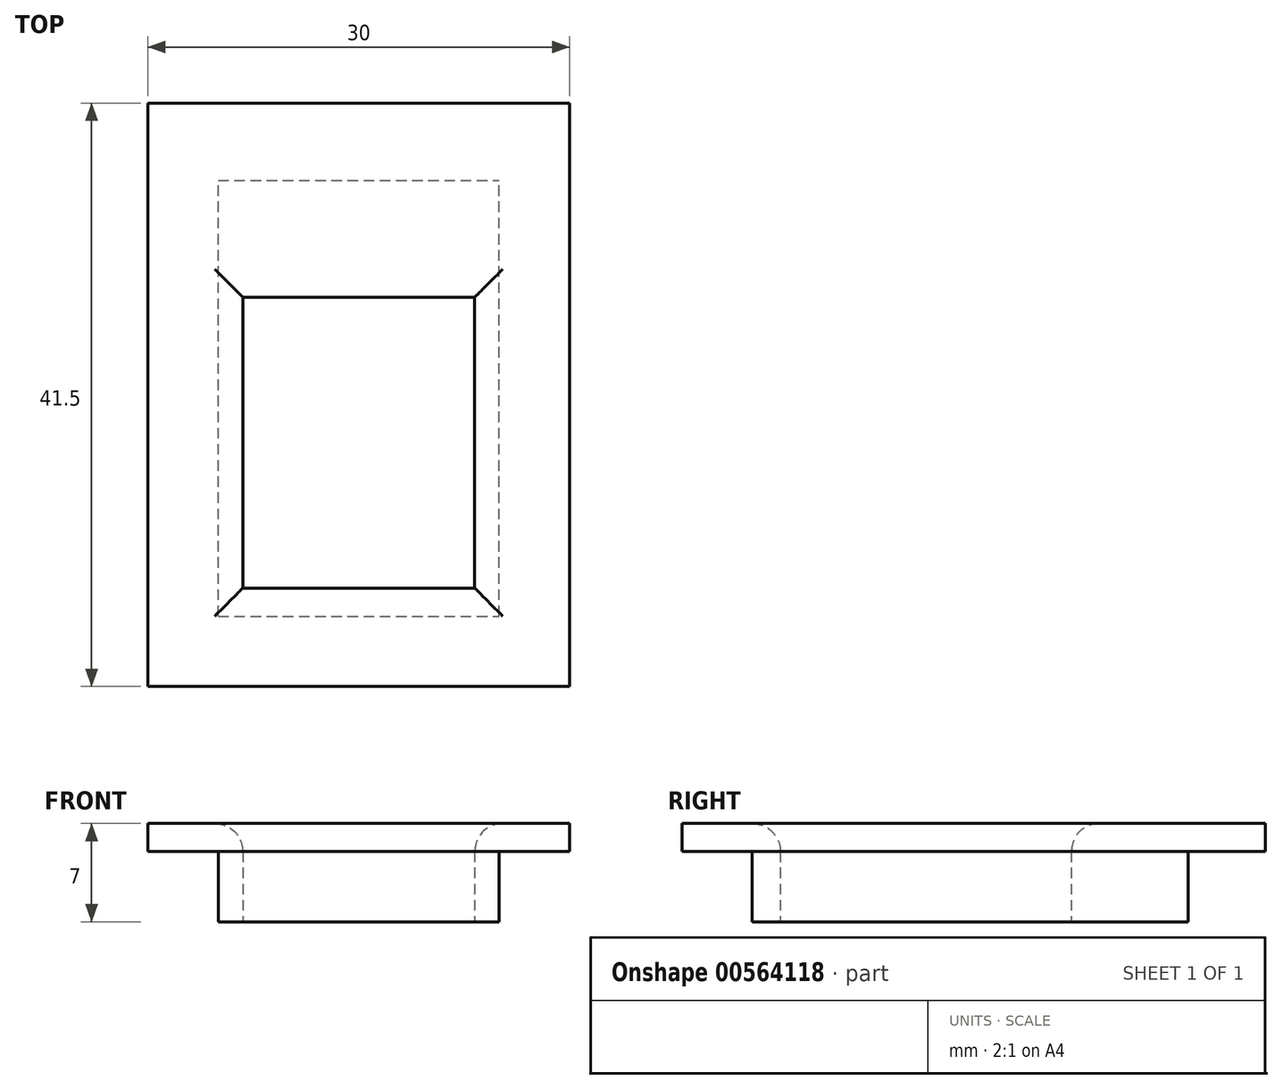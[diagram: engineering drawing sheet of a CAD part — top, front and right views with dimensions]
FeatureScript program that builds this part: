
annotation { "Feature Type Name" : "Feature", "Feature Type Description" : "" }
export const myFeature = defineFeature(function(context is Context, id is Id, definition is map)
    precondition{}
    {
        {
            var Q0;
            Q0=qCreatedBy(makeId("Top.planeOp"),FACE);
            var sketch = newSketch(context, id + "F0", { "sketchPlane" : qUnion([Q0])});
            skLineSegment(sketch, "E0.bottom", {"start": v(-14.79, 19.32) * mm, "end": v(15.21, 19.32) * mm});
            skLineSegment(sketch, "E0.top", {"start": v(-14.79, -22.18) * mm, "end": v(15.21, -22.18) * mm});
            skLineSegment(sketch, "E0.left", {"start": v(-14.79, 19.32) * mm, "end": v(-14.79, -22.18) * mm});
            skLineSegment(sketch, "E0.right", {"start": v(15.21, 19.32) * mm, "end": v(15.21, -22.18) * mm});
            skSolve(sketch);
        }
        {
            var Q0;
            Q0=makeQuery(id+"F0.imprint","IMPRINT",FACE,{"disambiguationData":[TD([[makeQuery(id+"F0.imprint","IMPRINT",EDGE,{"derivedFrom":sQuery(id+"F0.wireOp",EDGE,"E0.bottom")}),-1.0]])]});
            extrude(context, id + "F1", {"entities" : qUnion([Q0]), "depth" : 2 * mm, "offsetDistance" : 25 * mm});
        }
        {
            var Q0;
            Q0=makeQuery(id+"F1.opExtrude","CAP_FACE",FACE,{"disambiguationData":[OSD([sQuery(id+"F0.wireOp",EDGE,"E0.bottom"),sQuery(id+"F0.wireOp",EDGE,"E0.top"),sQuery(id+"F0.wireOp",EDGE,"E0.left"),sQuery(id+"F0.wireOp",EDGE,"E0.right")])],"isStart":true});
            var sketch = newSketch(context, id + "F2", { "sketchPlane" : qUnion([Q0])});
            skLineSegment(sketch, "E1.bottom", {"start": v(-9.79, 17.18) * mm, "end": v(10.21, 17.18) * mm});
            skLineSegment(sketch, "E1.top", {"start": v(-9.79, -13.82) * mm, "end": v(10.21, -13.82) * mm});
            skLineSegment(sketch, "E1.left", {"start": v(-9.79, 17.18) * mm, "end": v(-9.79, -13.82) * mm});
            skLineSegment(sketch, "E1.right", {"start": v(10.21, 17.18) * mm, "end": v(10.21, -13.82) * mm});
            skSolve(sketch);
        }
        {
            var Q0;
            Q0=makeQuery(id+"F2.imprint","IMPRINT",FACE,{"disambiguationData":[TD([[makeQuery(id+"F2.imprint","IMPRINT",EDGE,{"derivedFrom":sQuery(id+"F2.wireOp",EDGE,"E1.bottom")}),-1.0]])]});
            extrude(context, id + "F3", {"entities" : qUnion([Q0]), "operationType" : NewBodyOperationType.ADD, "depth" : 5 * mm, "offsetDistance" : 25 * mm});
        }
        {
            var Q0;
            Q0=makeQuery(id+"F3.opExtrude","CAP_FACE",FACE,{"disambiguationData":[OSD([sQuery(id+"F2.wireOp",EDGE,"E1.bottom"),sQuery(id+"F2.wireOp",EDGE,"E1.top"),sQuery(id+"F2.wireOp",EDGE,"E1.left"),sQuery(id+"F2.wireOp",EDGE,"E1.right")])],"isStart":false});
            var sketch = newSketch(context, id + "F4", { "sketchPlane" : qUnion([Q0])});
            skLineSegment(sketch, "E2.bottom", {"start": v(-8.04, 15.18) * mm, "end": v(8.46, 15.18) * mm});
            skLineSegment(sketch, "E2.top", {"start": v(-8.04, -5.52) * mm, "end": v(8.46, -5.52) * mm});
            skLineSegment(sketch, "E2.left", {"start": v(-8.04, 15.18) * mm, "end": v(-8.04, -5.52) * mm});
            skLineSegment(sketch, "E2.right", {"start": v(8.46, 15.18) * mm, "end": v(8.46, -5.52) * mm});
            skSolve(sketch);
        }
        {
            var Q0;
            Q0=makeQuery(id+"F4.imprint","IMPRINT",FACE,{"disambiguationData":[TD([[makeQuery(id+"F4.imprint","IMPRINT",EDGE,{"derivedFrom":sQuery(id+"F4.wireOp",EDGE,"E2.bottom")}),-1.0]])]});
            extrude(context, id + "F5", {"entities" : qUnion([Q0]), "operationType" : NewBodyOperationType.REMOVE, "oppositeDirection" : true, "depth" : 25 * mm, "offsetDistance" : 25 * mm});
        }
        {
            var Q0;
            Q0=makeQuery(id+"F5.boolean.opBoolean","INTERSECT",EDGE,{"derivedFrom":[makeQuery(id+"F1.opExtrude","CAP_FACE",FACE,{"disambiguationData":[OSD([sQuery(id+"F0.wireOp",EDGE,"E0.bottom"),sQuery(id+"F0.wireOp",EDGE,"E0.top"),sQuery(id+"F0.wireOp",EDGE,"E0.left"),sQuery(id+"F0.wireOp",EDGE,"E0.right")])],"isStart":false}),makeQuery(id+"F5.opExtrude","SWEPT_FACE",FACE,{"disambiguationData":[OSD([sQuery(id+"F4.wireOp",EDGE,"E2.right")])]})]});
            var Q1;
            Q1=makeQuery(id+"F5.boolean.opBoolean","INTERSECT",EDGE,{"derivedFrom":[makeQuery(id+"F1.opExtrude","CAP_FACE",FACE,{"disambiguationData":[OSD([sQuery(id+"F0.wireOp",EDGE,"E0.bottom"),sQuery(id+"F0.wireOp",EDGE,"E0.top"),sQuery(id+"F0.wireOp",EDGE,"E0.left"),sQuery(id+"F0.wireOp",EDGE,"E0.right")])],"isStart":false}),makeQuery(id+"F5.opExtrude","SWEPT_FACE",FACE,{"disambiguationData":[OSD([sQuery(id+"F4.wireOp",EDGE,"E2.top")])]})]});
            var Q2;
            Q2=makeQuery(id+"F5.boolean.opBoolean","INTERSECT",EDGE,{"derivedFrom":[makeQuery(id+"F1.opExtrude","CAP_FACE",FACE,{"disambiguationData":[OSD([sQuery(id+"F0.wireOp",EDGE,"E0.bottom"),sQuery(id+"F0.wireOp",EDGE,"E0.top"),sQuery(id+"F0.wireOp",EDGE,"E0.left"),sQuery(id+"F0.wireOp",EDGE,"E0.right")])],"isStart":false}),makeQuery(id+"F5.opExtrude","SWEPT_FACE",FACE,{"disambiguationData":[OSD([sQuery(id+"F4.wireOp",EDGE,"E2.left")])]})]});
            var Q3;
            Q3=makeQuery(id+"F5.boolean.opBoolean","INTERSECT",EDGE,{"derivedFrom":[makeQuery(id+"F1.opExtrude","CAP_FACE",FACE,{"disambiguationData":[OSD([sQuery(id+"F0.wireOp",EDGE,"E0.bottom"),sQuery(id+"F0.wireOp",EDGE,"E0.top"),sQuery(id+"F0.wireOp",EDGE,"E0.left"),sQuery(id+"F0.wireOp",EDGE,"E0.right")])],"isStart":false}),makeQuery(id+"F5.opExtrude","SWEPT_FACE",FACE,{"disambiguationData":[OSD([sQuery(id+"F4.wireOp",EDGE,"E2.bottom")])]})]});
            fillet(context, id + "F6", {"entities" : qUnion([Q0, Q1, Q2, Q3]), "radius" : 2 * mm, "tangentPropagation" : true, "allowEdgeOverflow" : false});
        }
    });
